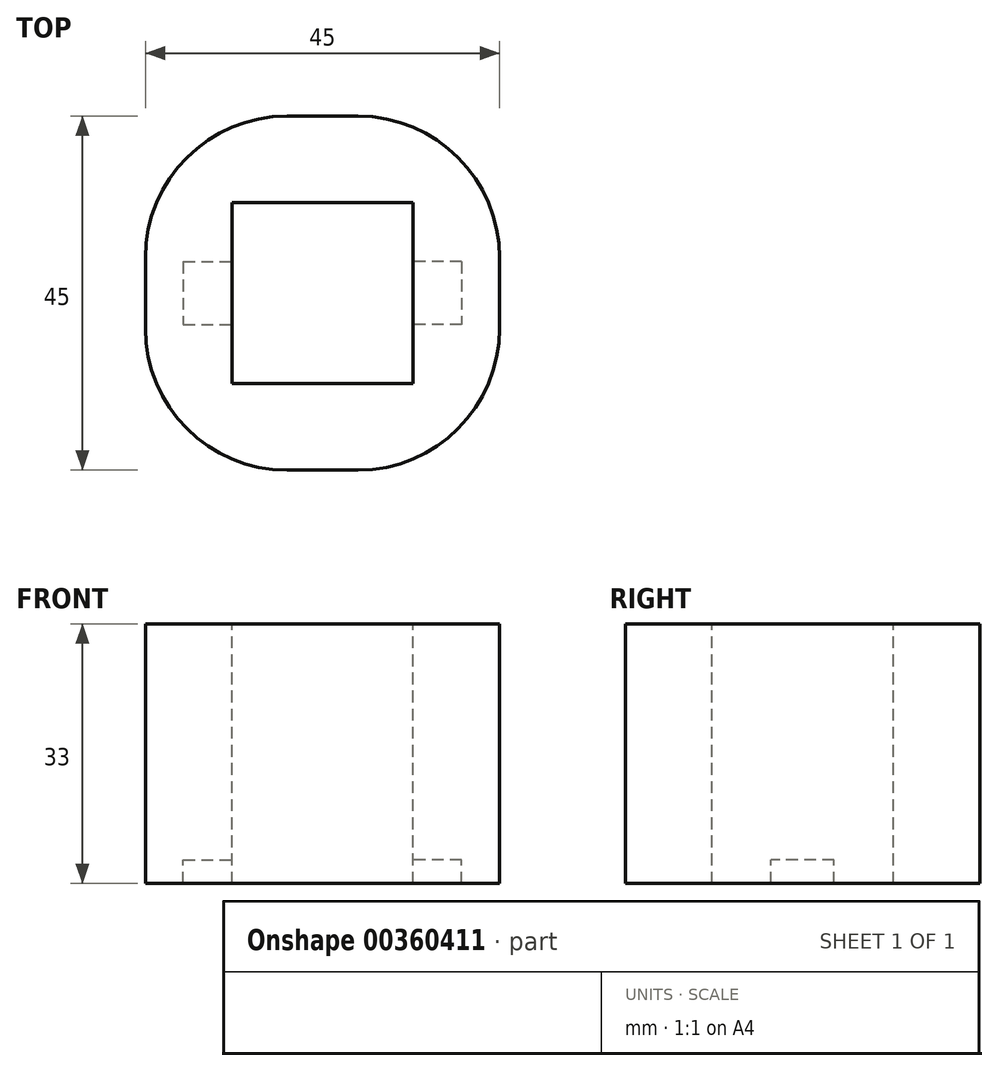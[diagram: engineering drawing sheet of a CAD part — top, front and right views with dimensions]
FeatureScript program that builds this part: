
annotation { "Feature Type Name" : "Feature", "Feature Type Description" : "" }
export const myFeature = defineFeature(function(context is Context, id is Id, definition is map)
    precondition{}
    {
        {
            var Q0;
            Q0=qCreatedBy(makeId("Top.planeOp"),FACE);
            var sketch = newSketch(context, id + "F0", { "sketchPlane" : qUnion([Q0])});
            skLineSegment(sketch, "E0.bottom", {"start": v(-22.5, 22.5) * mm, "end": v(22.5, 22.5) * mm});
            skLineSegment(sketch, "E0.top", {"start": v(-22.5, -22.5) * mm, "end": v(22.5, -22.5) * mm});
            skLineSegment(sketch, "E0.left", {"start": v(-22.5, 22.5) * mm, "end": v(-22.5, -22.5) * mm});
            skLineSegment(sketch, "E0.right", {"start": v(22.5, 22.5) * mm, "end": v(22.5, -22.5) * mm});
            skPoint(sketch, "E0.middle", {"position": v(0, 0) * mm});
            skSolve(sketch);
        }
        {
            var Q0;
            Q0 = qSketchRegion(id + "F0", true);
            extrude(context, id + "F1", {"entities" : qUnion([Q0]), "depth" : 3 * mm});
        }
        {
            var Q0;
            Q0=makeQuery(id+"F1.opExtrude","CAP_FACE",FACE,{"disambiguationData":[OSD([sQuery(id+"F0.wireOp",EDGE,"E0.bottom"),sQuery(id+"F0.wireOp",EDGE,"E0.top"),sQuery(id+"F0.wireOp",EDGE,"E0.left"),sQuery(id+"F0.wireOp",EDGE,"E0.right")])],"isStart":false});
            var sketch = newSketch(context, id + "F2", { "sketchPlane" : qUnion([Q0])});
            skLineSegment(sketch, "E1.bottom", {"start": v(-11.5, 11.5) * mm, "end": v(11.5, 11.5) * mm});
            skLineSegment(sketch, "E1.top", {"start": v(-11.5, -11.5) * mm, "end": v(11.5, -11.5) * mm});
            skLineSegment(sketch, "E1.left", {"start": v(-11.5, 11.5) * mm, "end": v(-11.5, 4) * mm});
            skLineSegment(sketch, "E1.right", {"start": v(11.5, 11.5) * mm, "end": v(11.5, 4) * mm});
            skPoint(sketch, "E1.middle", {"position": v(0, 0) * mm});
            skLineSegment(sketch, "E2.bottom", {"start": v(-17.68, 4) * mm, "end": v(-11.5, 4) * mm});
            skLineSegment(sketch, "E2.top", {"start": v(-17.68, -4) * mm, "end": v(-11.5, -4) * mm});
            skLineSegment(sketch, "E2.left", {"start": v(-17.68, 4) * mm, "end": v(-17.68, -4) * mm});
            skPoint(sketch, "E3.endSnap0", {"position": v(0, 11.5) * mm});
            skLineSegment(sketch, "E4.MirrorCS", {"start": v(17.68, 4) * mm, "end": v(11.5, 4) * mm});
            skLineSegment(sketch, "E5.MirrorCS", {"start": v(17.68, 4) * mm, "end": v(17.68, -4) * mm});
            skLineSegment(sketch, "E6.MirrorCS", {"start": v(17.68, -4) * mm, "end": v(11.5, -4) * mm});
            skLineSegment(sketch, "E7.trimOffspring", {"start": v(-11.5, -4) * mm, "end": v(-11.5, -11.5) * mm});
            skLineSegment(sketch, "E8.trimOffspring", {"start": v(11.5, -4) * mm, "end": v(11.5, -11.5) * mm});
            skSolve(sketch);
        }
        {
            var Q0;
            Q0 = qSketchRegion(id + "F2", true);
            extrude(context, id + "F3", {"entities" : qUnion([Q0]), "operationType" : NewBodyOperationType.REMOVE, "oppositeDirection" : true, "depth" : 25 * mm});
        }
        {
            var Q0;
            Q0=makeQuery(id+"F1.opExtrude","CAP_FACE",FACE,{"disambiguationData":[OSD([sQuery(id+"F0.wireOp",EDGE,"E0.bottom"),sQuery(id+"F0.wireOp",EDGE,"E0.top"),sQuery(id+"F0.wireOp",EDGE,"E0.left"),sQuery(id+"F0.wireOp",EDGE,"E0.right")])],"isStart":false});
            var sketch = newSketch(context, id + "F4", { "sketchPlane" : qUnion([Q0])});
            skLineSegment(sketch, "E9.bottom", {"start": v(-22.5, 22.5) * mm, "end": v(22.5, 22.5) * mm});
            skLineSegment(sketch, "E9.top", {"start": v(-22.5, -22.5) * mm, "end": v(22.5, -22.5) * mm});
            skLineSegment(sketch, "E9.left", {"start": v(-22.5, 22.5) * mm, "end": v(-22.5, -22.5) * mm});
            skLineSegment(sketch, "E9.right", {"start": v(22.5, 22.5) * mm, "end": v(22.5, -22.5) * mm});
            skSolve(sketch);
        }
        {
            var Q0;
            Q0 = qSketchRegion(id + "F4", true);
            extrude(context, id + "F5", {"entities" : qUnion([Q0]), "operationType" : NewBodyOperationType.ADD, "depth" : 5 * mm});
        }
        {
            var Q0;
            Q0=makeQuery(id+"F5.opExtrude","CAP_FACE",FACE,{"disambiguationData":[OSD([sQuery(id+"F4.wireOp",EDGE,"E9.bottom"),sQuery(id+"F4.wireOp",EDGE,"E9.top"),sQuery(id+"F4.wireOp",EDGE,"E9.left"),sQuery(id+"F4.wireOp",EDGE,"E9.right")])],"isStart":true});
            var sketch = newSketch(context, id + "F6", { "sketchPlane" : qUnion([Q0])});
            skLineSegment(sketch, "E10", {"start": v(11.5, -4) * mm, "end": v(11.5, 4) * mm});
            skLineSegment(sketch, "E11", {"start": v(-11.5, -4) * mm, "end": v(-11.5, 4) * mm});
            skSolve(sketch);
        }
        {
            var Q0;
            Q0=makeQuery(id+"F6.imprint","IMPRINT",FACE,{"disambiguationData":[TD([[makeQuery(id+"F6.imprint","IMPRINT",EDGE,{"derivedFrom":sQuery(id+"F6.wireOp",EDGE,"E10")}),1.0]])]});
            extrude(context, id + "F7", {"entities" : qUnion([Q0]), "operationType" : NewBodyOperationType.REMOVE, "oppositeDirection" : true, "depth" : 25 * mm});
        }
        {
            var Q0;
            Q0=makeQuery(id+"F5.boolean.opBoolean","MERGE",EDGE,{"derivedFrom":[makeQuery(id+"F1.opExtrude","SWEPT_EDGE",EDGE,{"disambiguationData":[OSD([sQuery(id+"F0.wireOp",EDGE,"E0.top"),sQuery(id+"F0.wireOp",EDGE,"E0.left")])]}),makeQuery(id+"F5.opExtrude","SWEPT_EDGE",EDGE,{"disambiguationData":[OSD([sQuery(id+"F4.wireOp",EDGE,"E9.top"),sQuery(id+"F4.wireOp",EDGE,"E9.left")])]})]});
            var Q1;
            Q1=makeQuery(id+"F5.boolean.opBoolean","MERGE",EDGE,{"derivedFrom":[makeQuery(id+"F1.opExtrude","SWEPT_EDGE",EDGE,{"disambiguationData":[OSD([sQuery(id+"F0.wireOp",EDGE,"E0.top"),sQuery(id+"F0.wireOp",EDGE,"E0.right")])]}),makeQuery(id+"F5.opExtrude","SWEPT_EDGE",EDGE,{"disambiguationData":[OSD([sQuery(id+"F4.wireOp",EDGE,"E9.top"),sQuery(id+"F4.wireOp",EDGE,"E9.right")])]})]});
            var Q2;
            Q2=makeQuery(id+"F5.boolean.opBoolean","MERGE",EDGE,{"derivedFrom":[makeQuery(id+"F1.opExtrude","SWEPT_EDGE",EDGE,{"disambiguationData":[OSD([sQuery(id+"F0.wireOp",EDGE,"E0.bottom"),sQuery(id+"F0.wireOp",EDGE,"E0.right")])]}),makeQuery(id+"F5.opExtrude","SWEPT_EDGE",EDGE,{"disambiguationData":[OSD([sQuery(id+"F4.wireOp",EDGE,"E9.bottom"),sQuery(id+"F4.wireOp",EDGE,"E9.right")])]})]});
            var Q3;
            Q3=makeQuery(id+"F5.boolean.opBoolean","MERGE",EDGE,{"derivedFrom":[makeQuery(id+"F1.opExtrude","SWEPT_EDGE",EDGE,{"disambiguationData":[OSD([sQuery(id+"F0.wireOp",EDGE,"E0.bottom"),sQuery(id+"F0.wireOp",EDGE,"E0.left")])]}),makeQuery(id+"F5.opExtrude","SWEPT_EDGE",EDGE,{"disambiguationData":[OSD([sQuery(id+"F4.wireOp",EDGE,"E9.bottom"),sQuery(id+"F4.wireOp",EDGE,"E9.left")])]})]});
            fillet(context, id + "F8", {"entities" : qUnion([Q0, Q1, Q2, Q3]), "radius" : 18 * mm, "tangentPropagation" : true, "allowEdgeOverflow" : false});
        }
        {
            var Q0;
            Q0=makeQuery(id+"F5.opExtrude","CAP_FACE",FACE,{"disambiguationData":[OSD([sQuery(id+"F4.wireOp",EDGE,"E9.bottom"),sQuery(id+"F4.wireOp",EDGE,"E9.top"),sQuery(id+"F4.wireOp",EDGE,"E9.left"),sQuery(id+"F4.wireOp",EDGE,"E9.right")])],"isStart":false});
            extrude(context, id + "F9", {"entities" : qUnion([Q0]), "operationType" : NewBodyOperationType.ADD, "depth" : 25 * mm});
        }
    });
